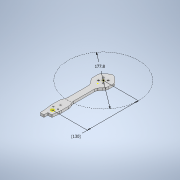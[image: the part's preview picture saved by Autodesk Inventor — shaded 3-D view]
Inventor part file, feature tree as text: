
AUTODESK INVENTOR PART (.ipt)
format: ipt  version: 2020 (Build 240168000, 168)  size: 250,880 bytes
history: native  units: in
note: dims shown in document units (in); Inventor stores cm internally (conversion verified against a paired STEP export)
features: sketch x3, extrude x2, fillet x2
ambient origin geometry x8: Origin, YZ Plane, XZ Plane, XY Plane, X Axis, Y Axis, Z Axis, Center Point
bodies: Body1 (feature_tree)
feature tree (7):
  extrude  "Extrusion1"  Depth=0.2362in
  sketch  "Sketch4"  dims[d7=0.4724in d8=5.1181in d9=7.0in d10=5.1181in]
  extrude  "Extrusion2"  Depth=5.1181in
  fillet  "Fillet2"  Radius=7.0in
  fillet  "Fillet3"  Radius=5.1181in
  sketch  "Sketch3"  dims[d2=0.2362in d3=0.0in d4=0.8352in]
  sketch  "Sketch5"  dims[d11=0.2992in d12=0.2992in d13=0.9835in d14=0.9835in d15=0.989in d16=0.1181in d17=0.0in d18=0.3937in d20=0.3937in d21=0.7874in]
